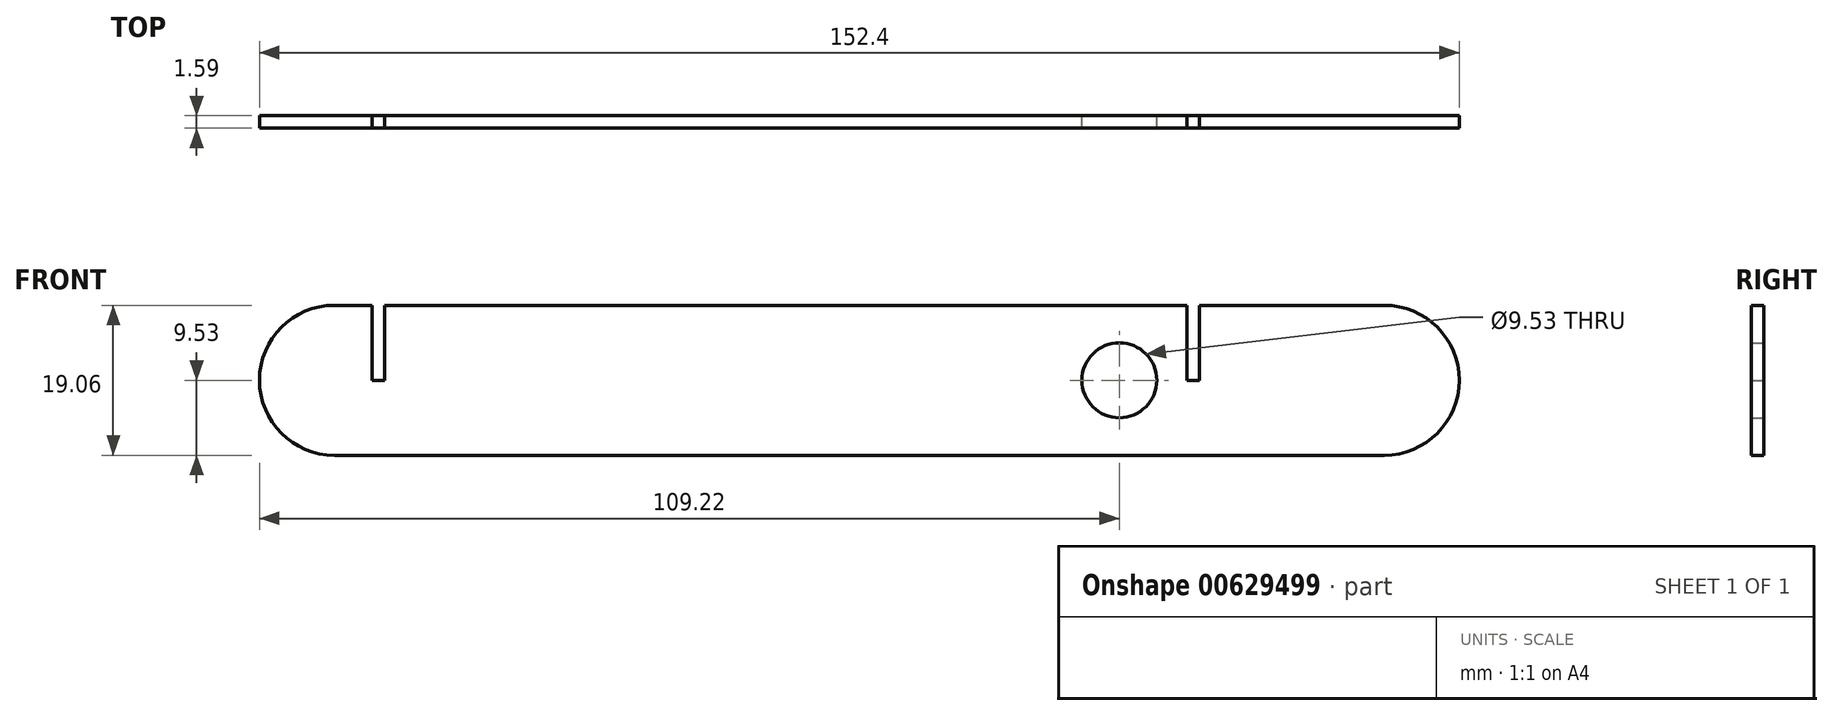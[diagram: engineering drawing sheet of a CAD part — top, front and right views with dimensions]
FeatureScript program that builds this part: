
annotation { "Feature Type Name" : "Feature", "Feature Type Description" : "" }
export const myFeature = defineFeature(function(context is Context, id is Id, definition is map)
    precondition{}
    {
        {
            var Q0;
            Q0=qCreatedBy(makeId("Front.planeOp"),FACE);
            var sketch = newSketch(context, id + "F0", { "sketchPlane" : qUnion([Q0])});
            skLineSegment(sketch, "E0.bottom", {"start": v(66.68, -9.52) * mm, "end": v(-66.68, -9.52) * mm});
            skLineSegment(sketch, "E0.top", {"start": v(66.68, 9.52) * mm, "end": v(-66.68, 9.52) * mm});
            skPoint(sketch, "E0.middle", {"position": v(0, 0) * mm});
            skArc(sketch, "E1", {"start": v(-66.68, 9.52) * mm, "mid": v(-76.2, 0) * mm, "end": v(-66.68, -9.52) * mm});
            skArc(sketch, "E2", {"start": v(66.68, -9.52) * mm, "mid": v(76.2, 0) * mm, "end": v(66.68, 9.52) * mm});
            skLineSegment(sketch, "E3", {"start": v(-61.91, 9.52) * mm, "end": v(-61.91, 0) * mm});
            skLineSegment(sketch, "E4", {"start": v(-61.91, 0) * mm, "end": v(-60.33, 0) * mm});
            skLineSegment(sketch, "E5", {"start": v(-60.33, 0) * mm, "end": v(-60.33, 9.52) * mm});
            skLineSegment(sketch, "E6", {"start": v(0, 0) * mm, "end": v(66.68, 0) * mm, "construction": true});
            skCircle(sketch, "E7", {"center": v(33.02, 0) * mm, "radius": 4.76 * mm});
            skLineSegment(sketch, "E8.bottom", {"start": v(43.18, 9.52) * mm, "end": v(41.6, 9.52) * mm});
            skLineSegment(sketch, "E8.top", {"start": v(43.18, 0) * mm, "end": v(41.6, 0) * mm});
            skLineSegment(sketch, "E8.left", {"start": v(43.18, 9.52) * mm, "end": v(43.18, 0) * mm});
            skLineSegment(sketch, "E8.right", {"start": v(41.6, 9.52) * mm, "end": v(41.6, 0) * mm});
            skSolve(sketch);
        }
        {
            var Q0;
            Q0=makeQuery(id+"F0.imprint","IMPRINT",FACE,{"disambiguationData":[TD([[makeQuery(id+"F0.imprint","IMPRINT",EDGE,{"derivedFrom":sQuery(id+"F0.wireOp",EDGE,"E0.bottom")}),-1.0]])]});
            extrude(context, id + "F1", {"entities" : qUnion([Q0]), "depth" : 1.59 * mm, "offsetDistance" : 25.4 * mm});
        }
    });
